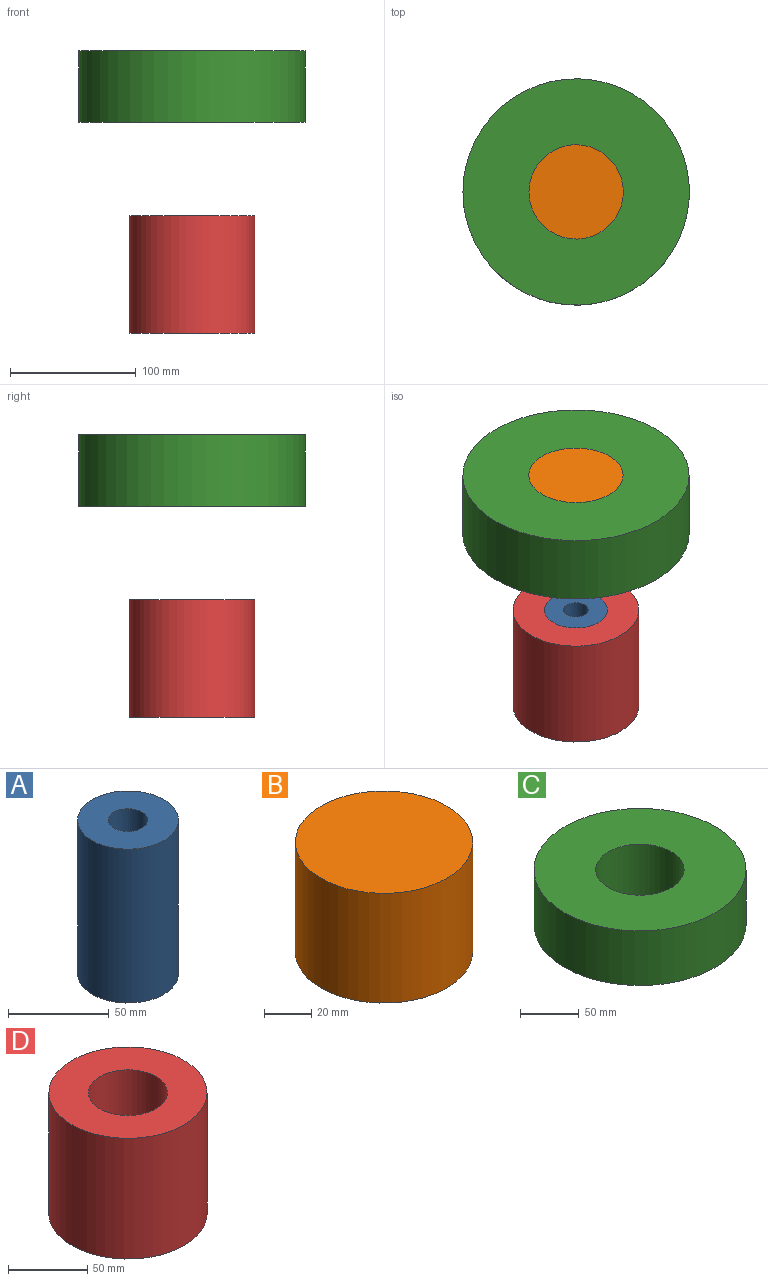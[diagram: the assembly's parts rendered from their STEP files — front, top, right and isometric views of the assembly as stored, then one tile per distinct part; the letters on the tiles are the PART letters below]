
ASSEMBLY  parts=4 mates=3
PART A: 6 faces, bbox 50x50x93.4 mm
  f0: cylinder r=6.4mm len=60.4mm, axis (0,0,-1), area 2428.7mm2, adj f1,f5
  f1: plane 50x50mm, normal (0,0,-1), area 1834.8mm2, adj f0,f2
  f2: cylinder r=25mm len=93.4mm, axis (0,0,-1), area 14671.2mm2, adj f1,f3
  f3: plane 50x50mm, normal (0,0,1), area 1664.8mm2, adj f2,f4
  f4: cylinder r=9.75mm len=27.2mm, axis (0,0,-1), area 1666.3mm2, adj f3,f5
  f5: cone r=6.4mm half-angle=30deg, axis (0,0,1), area 339.9mm2, adj f0,f4
PART B: 5 faces, bbox 75x75x56.8 mm
  f0: cylinder r=24.5mm len=49mm, axis (0,0,-1), area 1046.8mm2, adj f1,f4
  f1: plane 75x75mm, normal (0,0,-1), area 2532.1mm2, adj f0,f2
  f2: cylinder r=37.5mm len=75mm, axis (0,0,-1), area 13383.2mm2, adj f1,f3
  f3: plane 75x75mm, normal (0,0,1), area 4417.9mm2, adj f2
  f4: plane 49x49mm, normal (0,0,-1), area 1885.7mm2, adj f0
PART C: 4 faces, bbox 180x180x56.8 mm
  f0: cylinder r=37.5mm len=75mm, axis (0,0,-1), area 13383.2mm2, adj f1,f3
  f1: plane 180x180mm, normal (0,0,-1), area 21029mm2, adj f0,f2
  f2: cylinder r=90mm len=180mm, axis (0,0,-1), area 32119.6mm2, adj f1,f3
  f3: plane 180x180mm, normal (0,0,1), area 21029mm2, adj f0,f2
PART D: 4 faces, bbox 100x100x93.4 mm
  f0: cylinder r=25mm len=93.4mm, axis (0,0,-1), area 14671.2mm2, adj f1,f3
  f1: plane 100x100mm, normal (0,0,-1), area 5890.5mm2, adj f0,f2
  f2: cylinder r=50mm len=100mm, axis (0,0,-1), area 29342.5mm2, adj f1,f3
  f3: plane 100x100mm, normal (0,0,1), area 5890.5mm2, adj f0,f2
PLACE A at identity fixed
PLACE B t=(0,0,74.23)mm
PLACE C t=(0,0,74.23)mm
PLACE D at identity
MATE fastened D.f0 <-> A.f0  axis (0,0,-1) through (0,0,93.4)mm
MATE slider B.f0 <-> A.f0  axis (0,0,-1) through (0,0,167.63)mm
MATE fastened C.f0 <-> B.f0  axis (0,0,-1) through (0,0,224.43)mm
